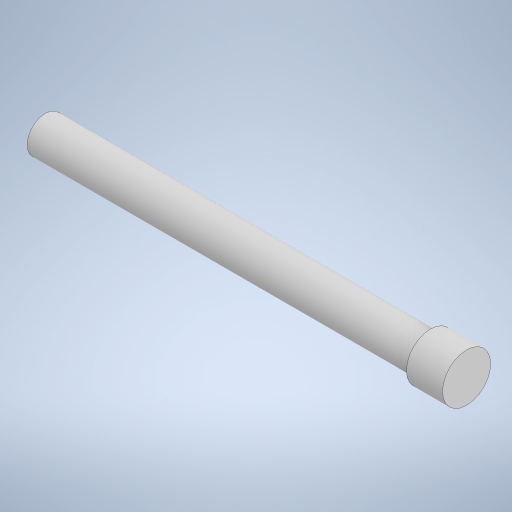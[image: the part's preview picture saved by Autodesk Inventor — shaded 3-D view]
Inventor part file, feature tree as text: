
AUTODESK INVENTOR PART (.ipt)
format: ipt  version: 2024 (Build 280153000, 153)  size: 226,304 bytes
history: native  units: in
note: dims shown in document units (in); Inventor stores cm internally (conversion verified against a paired STEP export)
features: extrude x2, sketch x2
ambient origin geometry x8: Origin, YZ Plane, XZ Plane, XY Plane, X Axis, Y Axis, Z Axis, Center Point
bodies: Solid1 (feature_tree)
feature tree (4):
  extrude  "Extrusion1"  Depth=2.0in TaperAngle=0.0deg
  extrude  "Extrusion2"  Depth=0.1875in TaperAngle=0.0deg
  sketch  "Sketch1"  dims[d0=0.19in d1=2.0in d2=0.0in]
  sketch  "Sketch2"  dims[d3=0.25in d4=0.1875in d5=0.0in]
